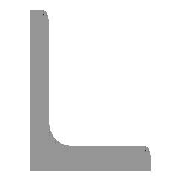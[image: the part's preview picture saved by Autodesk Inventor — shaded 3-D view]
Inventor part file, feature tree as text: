
AUTODESK INVENTOR PART (.ipt)
format: ipt  version: 2013 (Build 170138000, 138)  size: 129,536 bytes
history: native  units: mm (DEFAULTED — no unit token found)
features: other x4, plane x3, split x2, sketch x2
ambient origin geometry x8: Origin, YZ Plane, XZ Plane, XY Plane, X Axis, Y Axis, Z Axis, Center Point
bodies: Solid1 (feature_tree), Body (feature_tree)
feature tree (11):
  parser-record x1  (decoder bookkeeping rows leaked as tree rows — omitted from the tree; the rows remain in map.json)
  other  "Driven Length"
  other  "Start plane"
  other  "End plane"
  plane  "Work Plane4"
  split  "Split1"
  plane  "Work Plane5"
  split  "Split2"
  sketch  "Sketch3"  dims[d0=38.1mm]
  plane  "Work Plane3"
  sketch  "Sketch4"  dims[d1=38.1mm d2=4.7625mm d3=4.7625mm d4=1231.9mm d5=0.0mm d10=0.0mm d11=0.0mm d12=-0.0mm d13=1231.9mm d14=4.826mm d15=2.286mm d16=90.0deg d17=1231.9mm]
